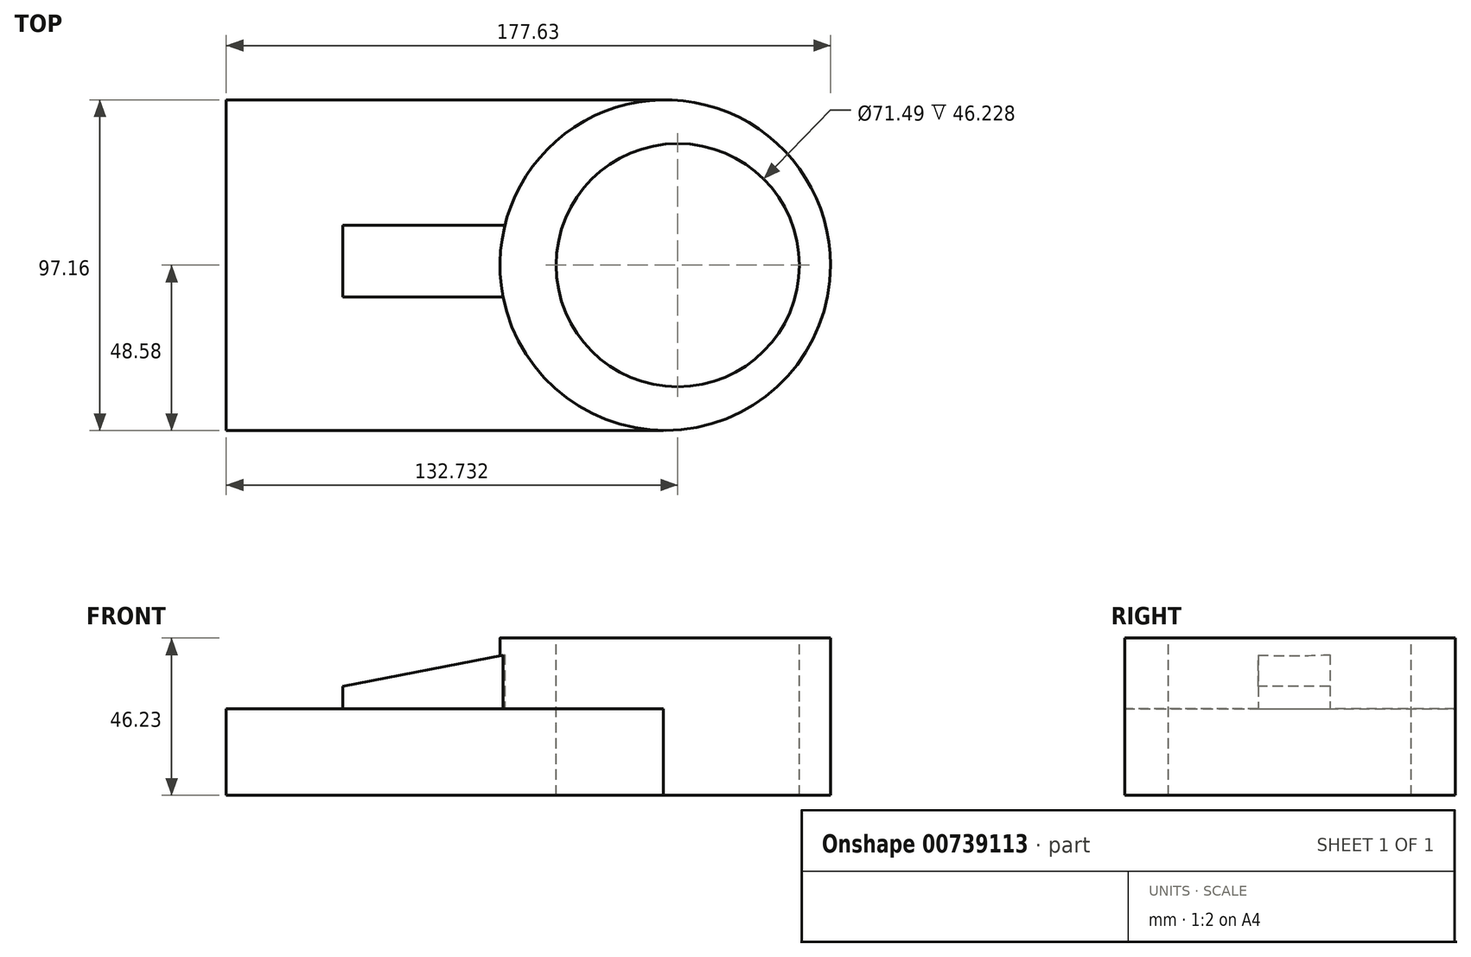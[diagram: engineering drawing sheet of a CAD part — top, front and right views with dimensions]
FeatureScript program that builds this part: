
annotation { "Feature Type Name" : "Feature", "Feature Type Description" : "" }
export const myFeature = defineFeature(function(context is Context, id is Id, definition is map)
    precondition{}
    {
        {
            var Q0;
            Q0=qCreatedBy(makeId("Top.planeOp"),FACE);
            var sketch = newSketch(context, id + "F0", { "sketchPlane" : qUnion([Q0])});
            skLineSegment(sketch, "E0.bottom", {"start": v(64.25, -48.58) * mm, "end": v(-64.25, -48.58) * mm});
            skLineSegment(sketch, "E0.top", {"start": v(64.25, 48.58) * mm, "end": v(-64.25, 48.58) * mm});
            skLineSegment(sketch, "E0.left", {"start": v(64.25, -48.58) * mm, "end": v(64.25, 48.58) * mm});
            skLineSegment(sketch, "E0.right", {"start": v(-64.25, -48.58) * mm, "end": v(-64.25, 48.58) * mm});
            skPoint(sketch, "E0.middle", {"position": v(0, 0) * mm});
            skSolve(sketch);
        }
        {
            var Q0;
            Q0=qCreatedBy(makeId("Top.planeOp"),FACE);
            var sketch = newSketch(context, id + "F1", { "sketchPlane" : qUnion([Q0])});
            skCircle(sketch, "E1", {"center": v(64.8, 0) * mm, "radius": 48.58 * mm});
            skSolve(sketch);
        }
        {
            var Q0;
            Q0 = qSketchRegion(id + "F0", true);
            extrude(context, id + "F2", {"entities" : qUnion([Q0]), "depth" : 25.4 * mm, "offsetDistance" : 25.4 * mm});
        }
        {
            var Q0;
            Q0 = qSketchRegion(id + "F1", true);
            extrude(context, id + "F3", {"entities" : qUnion([Q0]), "operationType" : NewBodyOperationType.ADD, "depth" : 46.23 * mm, "offsetDistance" : 25.4 * mm});
        }
        {
            var Q0;
            Q0=makeQuery(id+"F3.opExtrude","CAP_FACE",FACE,{"disambiguationData":[OSD([sQuery(id+"F1.wireOp",EDGE,"E1")])],"isStart":false});
            var sketch = newSketch(context, id + "F4", { "sketchPlane" : qUnion([Q0])});
            skCircle(sketch, "E2", {"center": v(68.48, 0) * mm, "radius": 35.75 * mm});
            skSolve(sketch);
        }
        {
            var Q0;
            Q0 = qSketchRegion(id + "F4", true);
            extrude(context, id + "F5", {"entities" : qUnion([Q0]), "operationType" : NewBodyOperationType.REMOVE, "oppositeDirection" : true, "depth" : 91.7 * mm, "offsetDistance" : 25.4 * mm});
        }
        {
            var Q0;
            Q0=makeQuery(id+"F2.opExtrude","CAP_EDGE",EDGE,{"disambiguationData":[OSD([sQuery(id+"F0.wireOp",EDGE,"E0.right")])],"isStart":false});
            cPlane(context, id + "F6", {"entities" : qUnion([Q0]), "cplaneType" : CPlaneType.LINE_ANGLE, "offset" : 25.4 * mm, "angle" : 169 * degree, "width" : 152.4 * mm, "height" : 152.4 * mm});
        }
        {
            var Q0;
            Q0=makeQuery(id+"F2.opExtrude","CAP_FACE",FACE,{"disambiguationData":[OSD([sQuery(id+"F0.wireOp",EDGE,"E0.bottom"),sQuery(id+"F0.wireOp",EDGE,"E0.top"),sQuery(id+"F0.wireOp",EDGE,"E0.left"),sQuery(id+"F0.wireOp",EDGE,"E0.right")])],"isStart":false});
            var sketch = newSketch(context, id + "F7", { "sketchPlane" : qUnion([Q0])});
            skLineSegment(sketch, "E3", {"start": v(17.12, -9.3) * mm, "end": v(-29.98, -9.3) * mm});
            skLineSegment(sketch, "E4", {"start": v(-29.98, -9.3) * mm, "end": v(-29.98, 11.75) * mm});
            skLineSegment(sketch, "E5", {"start": v(-29.98, 11.75) * mm, "end": v(17.67, 11.75) * mm});
            skSolve(sketch);
        }
        {
            var Q0;
            {var subQ0=sQuery(id+"F7.wireOp",EDGE,"E3");Q0=makeQuery(id+"F7.imprint","IMPRINT",FACE,{"disambiguationData":[TD([[makeQuery(id+"F7.imprint","IMPRINT",EDGE,{"derivedFrom":subQ0}),-1.0]])]});}
            var Q1;
            Q1=qCreatedBy(id+"F6.planeOp",FACE);
            extrude(context, id + "F8", {"entities" : qUnion([Q0]), "operationType" : NewBodyOperationType.ADD, "endBound" : BoundingType.UP_TO_SURFACE, "depth" : 25.4 * mm, "endBoundEntityFace" : qUnion([Q1]), "offsetDistance" : 25.4 * mm});
        }
    });
